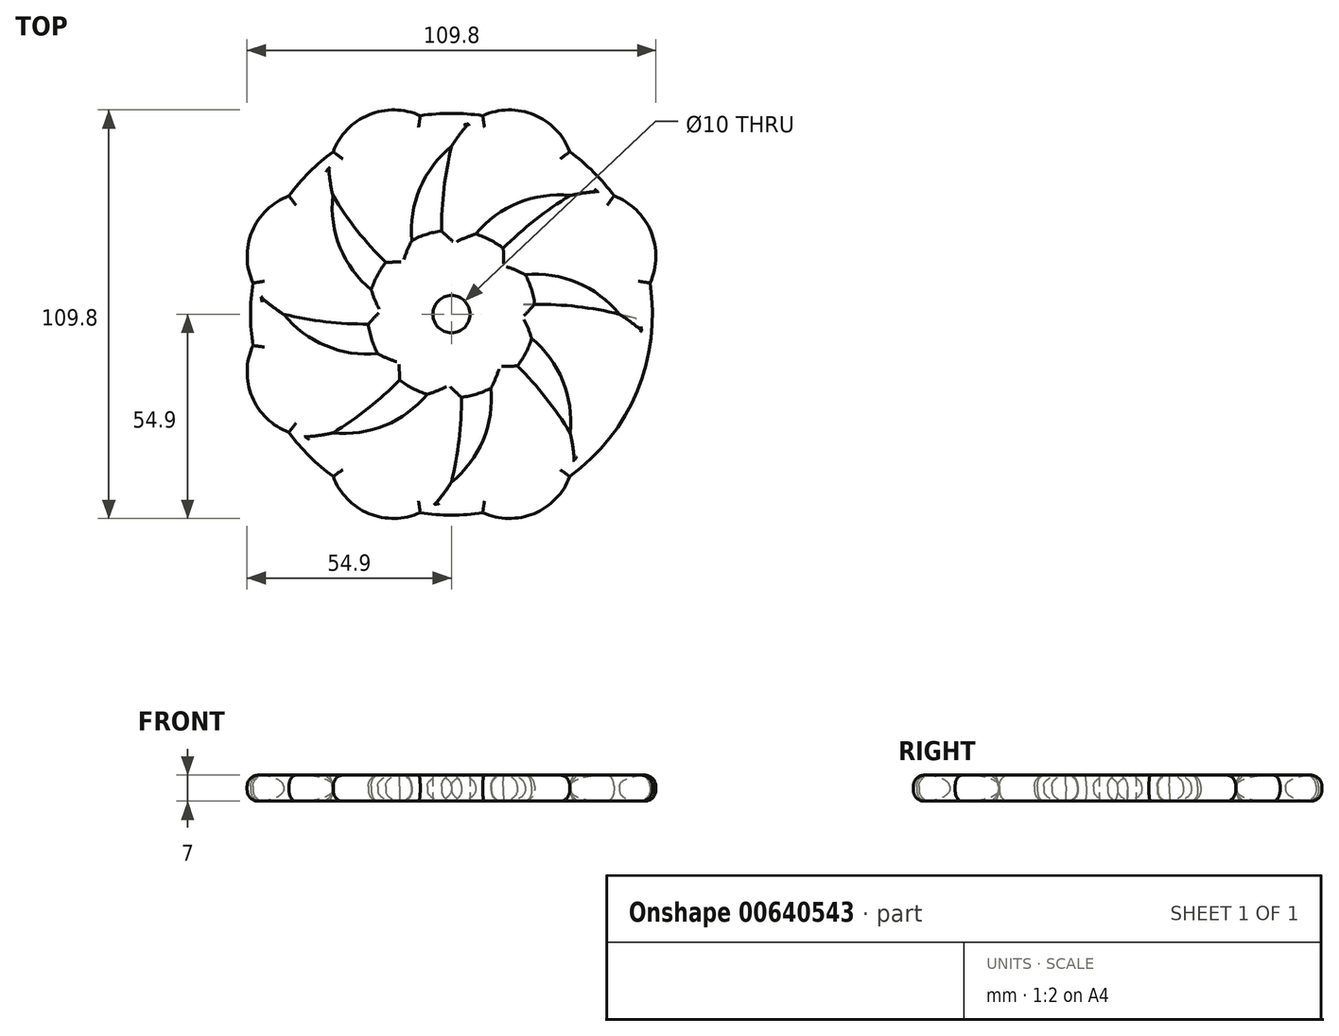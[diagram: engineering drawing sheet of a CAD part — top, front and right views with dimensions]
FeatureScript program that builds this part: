
annotation { "Feature Type Name" : "Feature", "Feature Type Description" : "" }
export const myFeature = defineFeature(function(context is Context, id is Id, definition is map)
    precondition{}
    {
        {
            var Q0;
            Q0=qCreatedBy(makeId("Top.planeOp"),FACE);
            var sketch = newSketch(context, id + "F0", { "sketchPlane" : qUnion([Q0])});
            skCircle(sketch, "E0", {"center": v(0, 0) * mm, "radius": 22.5 * mm});
            skPoint(sketch, "E1.center", {"position": v(-3, 0) * mm});
            skCircle(sketch, "E2", {"center": v(0, 0) * mm, "radius": 54 * mm});
            skCircle(sketch, "E3", {"center": v(0, 0) * mm, "radius": 5 * mm});
            skArc(sketch, "E4", {"start": v(0, 45.12) * mm, "mid": v(-10.75, 22.56) * mm, "end": v(0, 0) * mm});
            skArc(sketch, "E5", {"start": v(0, 45.12) * mm, "mid": v(-2.68, 22.56) * mm, "end": v(0, 0) * mm});
            skArc(sketch, "E6.1.0", {"start": v(-31.9, 31.9) * mm, "mid": v(-23.55, 8.35) * mm, "end": v(0, 0) * mm});
            skArc(sketch, "E6.1.1", {"start": v(-31.9, 31.9) * mm, "mid": v(-17.85, 14.06) * mm, "end": v(0, 0) * mm});
            skArc(sketch, "E6.2.0", {"start": v(-45.12, 0) * mm, "mid": v(-22.56, -10.75) * mm, "end": v(0, 0) * mm});
            skArc(sketch, "E6.2.1", {"start": v(-45.12, 0) * mm, "mid": v(-22.56, -2.68) * mm, "end": v(0, 0) * mm});
            skArc(sketch, "E6.3.0", {"start": v(-31.9, -31.9) * mm, "mid": v(-8.35, -23.55) * mm, "end": v(0, 0) * mm});
            skArc(sketch, "E6.3.1", {"start": v(-31.9, -31.9) * mm, "mid": v(-14.06, -17.85) * mm, "end": v(0, 0) * mm});
            skArc(sketch, "E6.4.0", {"start": v(0, -45.12) * mm, "mid": v(10.75, -22.56) * mm, "end": v(0, 0) * mm});
            skArc(sketch, "E6.4.1", {"start": v(0, -45.12) * mm, "mid": v(2.68, -22.56) * mm, "end": v(0, 0) * mm});
            skArc(sketch, "E6.5.0", {"start": v(31.9, -31.9) * mm, "mid": v(23.55, -8.35) * mm, "end": v(0, 0) * mm});
            skArc(sketch, "E6.5.1", {"start": v(31.9, -31.9) * mm, "mid": v(17.85, -14.06) * mm, "end": v(0, 0) * mm});
            skArc(sketch, "E6.6.0", {"start": v(45.12, 0) * mm, "mid": v(22.56, 10.75) * mm, "end": v(0, 0) * mm});
            skArc(sketch, "E6.6.1", {"start": v(45.12, 0) * mm, "mid": v(22.56, 2.68) * mm, "end": v(0, 0) * mm});
            skArc(sketch, "E6.7.0", {"start": v(31.9, 31.9) * mm, "mid": v(8.35, 23.55) * mm, "end": v(0, 0) * mm});
            skArc(sketch, "E6.7.1", {"start": v(31.9, 31.9) * mm, "mid": v(14.06, 17.85) * mm, "end": v(0, 0) * mm});
            skArc(sketch, "E7", {"start": v(-31.9, 31.9) * mm, "mid": v(-53.59, 22.2) * mm, "end": v(-45.12, 0) * mm});
            skArc(sketch, "E8.1.0", {"start": v(-45.12, 0) * mm, "mid": v(-53.59, -22.2) * mm, "end": v(-31.9, -31.9) * mm});
            skArc(sketch, "E8.2.0", {"start": v(-31.9, -31.9) * mm, "mid": v(-22.2, -53.59) * mm, "end": v(0, -45.12) * mm});
            skArc(sketch, "E8.3.0", {"start": v(0, -45.12) * mm, "mid": v(22.2, -53.59) * mm, "end": v(31.9, -31.9) * mm});
            skArc(sketch, "E8.4.0", {"start": v(31.9, -31.9) * mm, "mid": v(53.59, -22.2) * mm, "end": v(45.12, 0) * mm});
            skArc(sketch, "E8.5.0", {"start": v(45.12, 0) * mm, "mid": v(53.59, 22.2) * mm, "end": v(31.9, 31.9) * mm});
            skArc(sketch, "E8.6.0", {"start": v(31.9, 31.9) * mm, "mid": v(22.2, 53.59) * mm, "end": v(0, 45.12) * mm});
            skArc(sketch, "E8.7.0", {"start": v(0, 45.12) * mm, "mid": v(-22.2, 53.59) * mm, "end": v(-31.9, 31.9) * mm});
            skSolve(sketch);
        }
        {
            var Q0;
            {var subQ0=sQuery(id+"F0.wireOp",EDGE,"E7");var subQ1=sQuery(id+"F0.wireOp",EDGE,"E2");var subQ2=makeQuery(id+"F0.imprint","INTERSECT",VERTEX,{"disambiguationData":[OD(0.0)],"derivedFrom":[subQ1,subQ0]});Q0=makeQuery(id+"F0.imprint","IMPRINT",FACE,{"disambiguationData":[TD([[makeQuery(id+"F0.imprint","IMPRINT",EDGE,{"disambiguationData":[TD([[subQ2,-1.0]])],"derivedFrom":subQ1}),-1.0]])]});}
            var Q1;
            {var subQ3=sQuery(id+"F0.wireOp",EDGE,"E0");var subQ5=sQuery(id+"F0.wireOp",EDGE,"E6.1.0");var subQ9=makeQuery(id+"F0.imprint","INTERSECT",VERTEX,{"derivedFrom":[subQ3,subQ5]});Q1=makeQuery(id+"F0.imprint","IMPRINT",FACE,{"disambiguationData":[TD([[makeQuery(id+"F0.imprint","IMPRINT",EDGE,{"disambiguationData":[TD([[subQ9,-1.0]])],"derivedFrom":subQ3}),-1.0]])]});}
            var Q2;
            {var subQ0=sQuery(id+"F0.wireOp",EDGE,"E7");var subQ1=sQuery(id+"F0.wireOp",EDGE,"E2");var subQ2=makeQuery(id+"F0.imprint","INTERSECT",VERTEX,{"disambiguationData":[OD(1.0)],"derivedFrom":[subQ1,subQ0]});Q2=makeQuery(id+"F0.imprint","IMPRINT",FACE,{"disambiguationData":[TD([[makeQuery(id+"F0.imprint","IMPRINT",EDGE,{"disambiguationData":[TD([[subQ2,-1.0]])],"derivedFrom":subQ1}),1.0]])]});}
            var Q3;
            {var subQ1=sQuery(id+"F0.wireOp",EDGE,"E6.2.0");var subQ3=sQuery(id+"F0.wireOp",EDGE,"E0");var subQ4=makeQuery(id+"F0.imprint","INTERSECT",VERTEX,{"derivedFrom":[subQ3,subQ1]});Q3=makeQuery(id+"F0.imprint","IMPRINT",FACE,{"disambiguationData":[TD([[makeQuery(id+"F0.imprint","IMPRINT",EDGE,{"disambiguationData":[TD([[subQ4,-1.0]])],"derivedFrom":subQ3}),-1.0]])]});}
            var Q4;
            {var subQ0=sQuery(id+"F0.wireOp",EDGE,"E8.1.0");var subQ1=sQuery(id+"F0.wireOp",EDGE,"E2");var subQ2=makeQuery(id+"F0.imprint","INTERSECT",VERTEX,{"disambiguationData":[OD(0.0)],"derivedFrom":[subQ1,subQ0]});Q4=makeQuery(id+"F0.imprint","IMPRINT",FACE,{"disambiguationData":[TD([[makeQuery(id+"F0.imprint","IMPRINT",EDGE,{"disambiguationData":[TD([[subQ2,-1.0]])],"derivedFrom":subQ1}),-1.0]])]});}
            var Q5;
            {var subQ0=sQuery(id+"F0.wireOp",EDGE,"E6.2.0");var subQ1=sQuery(id+"F0.wireOp",EDGE,"E0");var subQ2=makeQuery(id+"F0.imprint","INTERSECT",VERTEX,{"derivedFrom":[subQ1,subQ0]});Q5=makeQuery(id+"F0.imprint","IMPRINT",FACE,{"disambiguationData":[TD([[makeQuery(id+"F0.imprint","IMPRINT",EDGE,{"disambiguationData":[TD([[subQ2,-1.0]])],"derivedFrom":subQ1}),1.0]])]});}
            var Q6;
            {var subQ0=sQuery(id+"F0.wireOp",EDGE,"E6.1.0");var subQ1=sQuery(id+"F0.wireOp",EDGE,"E0");var subQ2=makeQuery(id+"F0.imprint","INTERSECT",VERTEX,{"derivedFrom":[subQ1,subQ0]});Q6=makeQuery(id+"F0.imprint","IMPRINT",FACE,{"disambiguationData":[TD([[makeQuery(id+"F0.imprint","IMPRINT",EDGE,{"disambiguationData":[TD([[subQ2,-1.0]])],"derivedFrom":subQ1}),1.0]])]});}
            var Q7;
            {var subQ0=sQuery(id+"F0.wireOp",EDGE,"E4");var subQ1=sQuery(id+"F0.wireOp",EDGE,"E0");var subQ2=makeQuery(id+"F0.imprint","INTERSECT",VERTEX,{"derivedFrom":[subQ1,subQ0]});Q7=makeQuery(id+"F0.imprint","IMPRINT",FACE,{"disambiguationData":[TD([[makeQuery(id+"F0.imprint","IMPRINT",EDGE,{"disambiguationData":[TD([[subQ2,-1.0]])],"derivedFrom":subQ1}),1.0]])]});}
            var Q8;
            {var subQ3=sQuery(id+"F0.wireOp",EDGE,"E0");var subQ5=sQuery(id+"F0.wireOp",EDGE,"E4");var subQ7=makeQuery(id+"F0.imprint","INTERSECT",VERTEX,{"derivedFrom":[subQ3,subQ5]});Q8=makeQuery(id+"F0.imprint","IMPRINT",FACE,{"disambiguationData":[TD([[makeQuery(id+"F0.imprint","IMPRINT",EDGE,{"disambiguationData":[TD([[subQ7,-1.0]])],"derivedFrom":subQ3}),-1.0]])]});}
            var Q9;
            {var subQ0=sQuery(id+"F0.wireOp",EDGE,"E8.7.0");var subQ1=sQuery(id+"F0.wireOp",EDGE,"E2");var subQ2=makeQuery(id+"F0.imprint","INTERSECT",VERTEX,{"disambiguationData":[OD(0.0)],"derivedFrom":[subQ1,subQ0]});Q9=makeQuery(id+"F0.imprint","IMPRINT",FACE,{"disambiguationData":[TD([[makeQuery(id+"F0.imprint","IMPRINT",EDGE,{"disambiguationData":[TD([[subQ2,-1.0]])],"derivedFrom":subQ1}),-1.0]])]});}
            var Q10;
            {var subQ0=sQuery(id+"F0.wireOp",EDGE,"E8.6.0");var subQ1=sQuery(id+"F0.wireOp",EDGE,"E2");var subQ2=makeQuery(id+"F0.imprint","INTERSECT",VERTEX,{"disambiguationData":[OD(1.0)],"derivedFrom":[subQ1,subQ0]});Q10=makeQuery(id+"F0.imprint","IMPRINT",FACE,{"disambiguationData":[TD([[makeQuery(id+"F0.imprint","IMPRINT",EDGE,{"disambiguationData":[TD([[subQ2,-1.0]])],"derivedFrom":subQ1}),1.0]])]});}
            var Q11;
            {var subQ1=sQuery(id+"F0.wireOp",EDGE,"E6.7.0");var subQ3=sQuery(id+"F0.wireOp",EDGE,"E0");var subQ4=makeQuery(id+"F0.imprint","INTERSECT",VERTEX,{"derivedFrom":[subQ3,subQ1]});Q11=makeQuery(id+"F0.imprint","IMPRINT",FACE,{"disambiguationData":[TD([[makeQuery(id+"F0.imprint","IMPRINT",EDGE,{"disambiguationData":[TD([[subQ4,-1.0]])],"derivedFrom":subQ3}),-1.0]])]});}
            var Q12;
            {var subQ0=sQuery(id+"F0.wireOp",EDGE,"E8.6.0");var subQ1=sQuery(id+"F0.wireOp",EDGE,"E2");var subQ2=makeQuery(id+"F0.imprint","INTERSECT",VERTEX,{"disambiguationData":[OD(0.0)],"derivedFrom":[subQ1,subQ0]});Q12=makeQuery(id+"F0.imprint","IMPRINT",FACE,{"disambiguationData":[TD([[makeQuery(id+"F0.imprint","IMPRINT",EDGE,{"disambiguationData":[TD([[subQ2,-1.0]])],"derivedFrom":subQ1}),-1.0]])]});}
            var Q13;
            {var subQ0=sQuery(id+"F0.wireOp",EDGE,"E8.5.0");var subQ1=sQuery(id+"F0.wireOp",EDGE,"E2");var subQ2=makeQuery(id+"F0.imprint","INTERSECT",VERTEX,{"disambiguationData":[OD(0.0)],"derivedFrom":[subQ1,subQ0]});Q13=makeQuery(id+"F0.imprint","IMPRINT",FACE,{"disambiguationData":[TD([[makeQuery(id+"F0.imprint","IMPRINT",EDGE,{"disambiguationData":[TD([[subQ2,-1.0]])],"derivedFrom":subQ1}),1.0]])]});}
            var Q14;
            {var subQ0=sQuery(id+"F0.wireOp",EDGE,"E8.5.0");var subQ1=sQuery(id+"F0.wireOp",EDGE,"E2");var subQ2=makeQuery(id+"F0.imprint","INTERSECT",VERTEX,{"disambiguationData":[OD(0.0)],"derivedFrom":[subQ1,subQ0]});Q14=makeQuery(id+"F0.imprint","IMPRINT",FACE,{"disambiguationData":[TD([[makeQuery(id+"F0.imprint","IMPRINT",EDGE,{"disambiguationData":[TD([[subQ2,1.0]])],"derivedFrom":subQ1}),-1.0]])]});}
            var Q15;
            {var subQ0=sQuery(id+"F0.wireOp",EDGE,"E8.5.0");var subQ1=sQuery(id+"F0.wireOp",EDGE,"E2");var subQ2=makeQuery(id+"F0.imprint","INTERSECT",VERTEX,{"disambiguationData":[OD(1.0)],"derivedFrom":[subQ1,subQ0]});Q15=makeQuery(id+"F0.imprint","IMPRINT",FACE,{"disambiguationData":[TD([[makeQuery(id+"F0.imprint","IMPRINT",EDGE,{"disambiguationData":[TD([[subQ2,1.0]])],"derivedFrom":subQ1}),1.0]])]});}
            var Q16;
            {var subQ0=sQuery(id+"F0.wireOp",EDGE,"E8.4.0");var subQ1=sQuery(id+"F0.wireOp",EDGE,"E2");var subQ2=makeQuery(id+"F0.imprint","INTERSECT",VERTEX,{"disambiguationData":[OD(0.0)],"derivedFrom":[subQ1,subQ0]});Q16=makeQuery(id+"F0.imprint","IMPRINT",FACE,{"disambiguationData":[TD([[makeQuery(id+"F0.imprint","IMPRINT",EDGE,{"disambiguationData":[TD([[subQ2,-1.0]])],"derivedFrom":subQ1}),-1.0]])]});}
            var Q17;
            {var subQ0=sQuery(id+"F0.wireOp",EDGE,"E8.3.0");var subQ1=sQuery(id+"F0.wireOp",EDGE,"E2");var subQ2=makeQuery(id+"F0.imprint","INTERSECT",VERTEX,{"disambiguationData":[OD(1.0)],"derivedFrom":[subQ1,subQ0]});Q17=makeQuery(id+"F0.imprint","IMPRINT",FACE,{"disambiguationData":[TD([[makeQuery(id+"F0.imprint","IMPRINT",EDGE,{"disambiguationData":[TD([[subQ2,-1.0]])],"derivedFrom":subQ1}),1.0]])]});}
            var Q18;
            {var subQ0=sQuery(id+"F0.wireOp",EDGE,"E8.3.0");var subQ1=sQuery(id+"F0.wireOp",EDGE,"E2");var subQ2=makeQuery(id+"F0.imprint","INTERSECT",VERTEX,{"disambiguationData":[OD(0.0)],"derivedFrom":[subQ1,subQ0]});Q18=makeQuery(id+"F0.imprint","IMPRINT",FACE,{"disambiguationData":[TD([[makeQuery(id+"F0.imprint","IMPRINT",EDGE,{"disambiguationData":[TD([[subQ2,-1.0]])],"derivedFrom":subQ1}),-1.0]])]});}
            var Q19;
            {var subQ0=sQuery(id+"F0.wireOp",EDGE,"E8.2.0");var subQ1=sQuery(id+"F0.wireOp",EDGE,"E2");var subQ2=makeQuery(id+"F0.imprint","INTERSECT",VERTEX,{"disambiguationData":[OD(1.0)],"derivedFrom":[subQ1,subQ0]});Q19=makeQuery(id+"F0.imprint","IMPRINT",FACE,{"disambiguationData":[TD([[makeQuery(id+"F0.imprint","IMPRINT",EDGE,{"disambiguationData":[TD([[subQ2,-1.0]])],"derivedFrom":subQ1}),1.0]])]});}
            var Q20;
            {var subQ0=sQuery(id+"F0.wireOp",EDGE,"E8.2.0");var subQ1=sQuery(id+"F0.wireOp",EDGE,"E2");var subQ2=makeQuery(id+"F0.imprint","INTERSECT",VERTEX,{"disambiguationData":[OD(0.0)],"derivedFrom":[subQ1,subQ0]});Q20=makeQuery(id+"F0.imprint","IMPRINT",FACE,{"disambiguationData":[TD([[makeQuery(id+"F0.imprint","IMPRINT",EDGE,{"disambiguationData":[TD([[subQ2,-1.0]])],"derivedFrom":subQ1}),-1.0]])]});}
            var Q21;
            {var subQ3=sQuery(id+"F0.wireOp",EDGE,"E0");var subQ5=sQuery(id+"F0.wireOp",EDGE,"E6.3.0");var subQ7=makeQuery(id+"F0.imprint","INTERSECT",VERTEX,{"derivedFrom":[subQ3,subQ5]});Q21=makeQuery(id+"F0.imprint","IMPRINT",FACE,{"disambiguationData":[TD([[makeQuery(id+"F0.imprint","IMPRINT",EDGE,{"disambiguationData":[TD([[subQ7,-1.0]])],"derivedFrom":subQ3}),-1.0]])]});}
            var Q22;
            {var subQ0=sQuery(id+"F0.wireOp",EDGE,"E8.1.0");var subQ1=sQuery(id+"F0.wireOp",EDGE,"E2");var subQ2=makeQuery(id+"F0.imprint","INTERSECT",VERTEX,{"disambiguationData":[OD(1.0)],"derivedFrom":[subQ1,subQ0]});Q22=makeQuery(id+"F0.imprint","IMPRINT",FACE,{"disambiguationData":[TD([[makeQuery(id+"F0.imprint","IMPRINT",EDGE,{"disambiguationData":[TD([[subQ2,-1.0]])],"derivedFrom":subQ1}),1.0]])]});}
            var Q23;
            {var subQ3=sQuery(id+"F0.wireOp",EDGE,"E0");var subQ5=sQuery(id+"F0.wireOp",EDGE,"E6.4.0");var subQ7=makeQuery(id+"F0.imprint","INTERSECT",VERTEX,{"derivedFrom":[subQ3,subQ5]});Q23=makeQuery(id+"F0.imprint","IMPRINT",FACE,{"disambiguationData":[TD([[makeQuery(id+"F0.imprint","IMPRINT",EDGE,{"disambiguationData":[TD([[subQ7,-1.0]])],"derivedFrom":subQ3}),-1.0]])]});}
            var Q24;
            {var subQ1=sQuery(id+"F0.wireOp",EDGE,"E6.6.1");var subQ3=sQuery(id+"F0.wireOp",EDGE,"E0");var subQ4=makeQuery(id+"F0.imprint","INTERSECT",VERTEX,{"derivedFrom":[subQ3,subQ1]});Q24=makeQuery(id+"F0.imprint","IMPRINT",FACE,{"disambiguationData":[TD([[makeQuery(id+"F0.imprint","IMPRINT",EDGE,{"disambiguationData":[TD([[subQ4,1.0]])],"derivedFrom":subQ3}),-1.0]])]});}
            var Q25;
            {var subQ3=sQuery(id+"F0.wireOp",EDGE,"E0");var subQ8=sQuery(id+"F0.wireOp",EDGE,"E6.6.0");var subQ10=makeQuery(id+"F0.imprint","INTERSECT",VERTEX,{"derivedFrom":[subQ3,subQ8]});Q25=makeQuery(id+"F0.imprint","IMPRINT",FACE,{"disambiguationData":[TD([[makeQuery(id+"F0.imprint","IMPRINT",EDGE,{"disambiguationData":[TD([[subQ10,-1.0]])],"derivedFrom":subQ3}),-1.0]])]});}
            var Q26;
            {var subQ0=sQuery(id+"F0.wireOp",EDGE,"E6.3.0");var subQ1=sQuery(id+"F0.wireOp",EDGE,"E0");var subQ2=makeQuery(id+"F0.imprint","INTERSECT",VERTEX,{"derivedFrom":[subQ1,subQ0]});Q26=makeQuery(id+"F0.imprint","IMPRINT",FACE,{"disambiguationData":[TD([[makeQuery(id+"F0.imprint","IMPRINT",EDGE,{"disambiguationData":[TD([[subQ2,-1.0]])],"derivedFrom":subQ1}),1.0]])]});}
            var Q27;
            {var subQ0=sQuery(id+"F0.wireOp",EDGE,"E6.4.0");var subQ1=sQuery(id+"F0.wireOp",EDGE,"E0");var subQ2=makeQuery(id+"F0.imprint","INTERSECT",VERTEX,{"derivedFrom":[subQ1,subQ0]});Q27=makeQuery(id+"F0.imprint","IMPRINT",FACE,{"disambiguationData":[TD([[makeQuery(id+"F0.imprint","IMPRINT",EDGE,{"disambiguationData":[TD([[subQ2,-1.0]])],"derivedFrom":subQ1}),1.0]])]});}
            var Q28;
            {var subQ0=sQuery(id+"F0.wireOp",EDGE,"E6.6.1");var subQ1=sQuery(id+"F0.wireOp",EDGE,"E0");var subQ2=makeQuery(id+"F0.imprint","INTERSECT",VERTEX,{"derivedFrom":[subQ1,subQ0]});Q28=makeQuery(id+"F0.imprint","IMPRINT",FACE,{"disambiguationData":[TD([[makeQuery(id+"F0.imprint","IMPRINT",EDGE,{"disambiguationData":[TD([[subQ2,1.0]])],"derivedFrom":subQ1}),1.0]])]});}
            var Q29;
            {var subQ0=sQuery(id+"F0.wireOp",EDGE,"E6.6.0");var subQ1=sQuery(id+"F0.wireOp",EDGE,"E0");var subQ2=makeQuery(id+"F0.imprint","INTERSECT",VERTEX,{"derivedFrom":[subQ1,subQ0]});Q29=makeQuery(id+"F0.imprint","IMPRINT",FACE,{"disambiguationData":[TD([[makeQuery(id+"F0.imprint","IMPRINT",EDGE,{"disambiguationData":[TD([[subQ2,-1.0]])],"derivedFrom":subQ1}),1.0]])]});}
            var Q30;
            {var subQ0=sQuery(id+"F0.wireOp",EDGE,"E6.7.0");var subQ1=sQuery(id+"F0.wireOp",EDGE,"E0");var subQ2=makeQuery(id+"F0.imprint","INTERSECT",VERTEX,{"derivedFrom":[subQ1,subQ0]});Q30=makeQuery(id+"F0.imprint","IMPRINT",FACE,{"disambiguationData":[TD([[makeQuery(id+"F0.imprint","IMPRINT",EDGE,{"disambiguationData":[TD([[subQ2,-1.0]])],"derivedFrom":subQ1}),1.0]])]});}
            var Q31;
            {var subQ0=sQuery(id+"F0.wireOp",EDGE,"E6.1.1");var subQ1=sQuery(id+"F0.wireOp",EDGE,"E0");var subQ2=makeQuery(id+"F0.imprint","INTERSECT",VERTEX,{"derivedFrom":[subQ1,subQ0]});Q31=makeQuery(id+"F0.imprint","IMPRINT",FACE,{"disambiguationData":[TD([[makeQuery(id+"F0.imprint","IMPRINT",EDGE,{"disambiguationData":[TD([[subQ2,-1.0]])],"derivedFrom":subQ1}),1.0]])]});}
            var Q32;
            {var subQ0=sQuery(id+"F0.wireOp",EDGE,"E6.4.1");var subQ1=sQuery(id+"F0.wireOp",EDGE,"E0");var subQ2=makeQuery(id+"F0.imprint","INTERSECT",VERTEX,{"derivedFrom":[subQ1,subQ0]});Q32=makeQuery(id+"F0.imprint","IMPRINT",FACE,{"disambiguationData":[TD([[makeQuery(id+"F0.imprint","IMPRINT",EDGE,{"disambiguationData":[TD([[subQ2,-1.0]])],"derivedFrom":subQ1}),1.0]])]});}
            var Q33;
            {var subQ0=sQuery(id+"F0.wireOp",EDGE,"E5");var subQ1=sQuery(id+"F0.wireOp",EDGE,"E0");var subQ2=makeQuery(id+"F0.imprint","INTERSECT",VERTEX,{"derivedFrom":[subQ1,subQ0]});Q33=makeQuery(id+"F0.imprint","IMPRINT",FACE,{"disambiguationData":[TD([[makeQuery(id+"F0.imprint","IMPRINT",EDGE,{"disambiguationData":[TD([[subQ2,-1.0]])],"derivedFrom":subQ1}),1.0]])]});}
            var Q34;
            {var subQ0=sQuery(id+"F0.wireOp",EDGE,"E6.7.1");var subQ1=sQuery(id+"F0.wireOp",EDGE,"E0");var subQ2=makeQuery(id+"F0.imprint","INTERSECT",VERTEX,{"derivedFrom":[subQ1,subQ0]});Q34=makeQuery(id+"F0.imprint","IMPRINT",FACE,{"disambiguationData":[TD([[makeQuery(id+"F0.imprint","IMPRINT",EDGE,{"disambiguationData":[TD([[subQ2,-1.0]])],"derivedFrom":subQ1}),1.0]])]});}
            var Q35;
            {var subQ0=sQuery(id+"F0.wireOp",EDGE,"E6.5.1");var subQ1=sQuery(id+"F0.wireOp",EDGE,"E0");var subQ2=makeQuery(id+"F0.imprint","INTERSECT",VERTEX,{"derivedFrom":[subQ1,subQ0]});Q35=makeQuery(id+"F0.imprint","IMPRINT",FACE,{"disambiguationData":[TD([[makeQuery(id+"F0.imprint","IMPRINT",EDGE,{"disambiguationData":[TD([[subQ2,-1.0]])],"derivedFrom":subQ1}),1.0]])]});}
            var Q36;
            {var subQ0=sQuery(id+"F0.wireOp",EDGE,"E6.3.1");var subQ1=sQuery(id+"F0.wireOp",EDGE,"E0");var subQ2=makeQuery(id+"F0.imprint","INTERSECT",VERTEX,{"derivedFrom":[subQ1,subQ0]});Q36=makeQuery(id+"F0.imprint","IMPRINT",FACE,{"disambiguationData":[TD([[makeQuery(id+"F0.imprint","IMPRINT",EDGE,{"disambiguationData":[TD([[subQ2,-1.0]])],"derivedFrom":subQ1}),1.0]])]});}
            var Q37;
            {var subQ0=sQuery(id+"F0.wireOp",EDGE,"E6.2.1");var subQ1=sQuery(id+"F0.wireOp",EDGE,"E0");var subQ2=makeQuery(id+"F0.imprint","INTERSECT",VERTEX,{"derivedFrom":[subQ1,subQ0]});Q37=makeQuery(id+"F0.imprint","IMPRINT",FACE,{"disambiguationData":[TD([[makeQuery(id+"F0.imprint","IMPRINT",EDGE,{"disambiguationData":[TD([[subQ2,-1.0]])],"derivedFrom":subQ1}),1.0]])]});}
            var Q38;
            {var subQ0=sQuery(id+"F0.wireOp",EDGE,"E6.6.0");var subQ1=sQuery(id+"F0.wireOp",EDGE,"E0");var subQ2=makeQuery(id+"F0.imprint","INTERSECT",VERTEX,{"derivedFrom":[subQ1,subQ0]});Q38=makeQuery(id+"F0.imprint","IMPRINT",FACE,{"disambiguationData":[TD([[makeQuery(id+"F0.imprint","IMPRINT",EDGE,{"disambiguationData":[TD([[subQ2,1.0]])],"derivedFrom":subQ1}),1.0]])]});}
            var Q39;
            {var subQ0=sQuery(id+"F0.wireOp",EDGE,"E8.7.0");var subQ1=sQuery(id+"F0.wireOp",EDGE,"E2");var subQ2=makeQuery(id+"F0.imprint","INTERSECT",VERTEX,{"disambiguationData":[OD(1.0)],"derivedFrom":[subQ1,subQ0]});Q39=makeQuery(id+"F0.imprint","IMPRINT",FACE,{"disambiguationData":[TD([[makeQuery(id+"F0.imprint","IMPRINT",EDGE,{"disambiguationData":[TD([[subQ2,-1.0]])],"derivedFrom":subQ1}),1.0]])]});}
            extrude(context, id + "F1", {"entities" : qUnion([Q0, Q1, Q2, Q3, Q4, Q5, Q6, Q7, Q8, Q9, Q10, Q11, Q12, Q13, Q14, Q15, Q16, Q17, Q18, Q19, Q20, Q21, Q22, Q23, Q24, Q25, Q26, Q27, Q28, Q29, Q30, Q31, Q32, Q33, Q34, Q35, Q36, Q37, Q38, Q39]), "depth" : 7 * mm, "offsetDistance" : 25 * mm});
        }
        {
            var Q0;
            {var subQ0=sQuery(id+"F0.wireOp",EDGE,"E2");Q0=makeQuery(id+"F1.opExtrude","CAP_EDGE",EDGE,{"disambiguationData":[OSD([subQ0]),TDD([makeQuery(id+"F0.imprint","IMPRINT",EDGE,{"disambiguationData":[TD([[makeQuery(id+"F0.imprint","INTERSECT",VERTEX,{"disambiguationData":[OD(1.0)],"derivedFrom":[subQ0,sQuery(id+"F0.wireOp",EDGE,"E8.7.0")]}),-1.0]])],"derivedFrom":subQ0})])],"isStart":false});}
            var Q1;
            Q1=makeQuery(id+"F1.opExtrude","CAP_EDGE",EDGE,{"disambiguationData":[OSD([sQuery(id+"F0.wireOp",EDGE,"E8.7.0")])],"isStart":false});
            var Q2;
            {var subQ0=sQuery(id+"F0.wireOp",EDGE,"E2");Q2=makeQuery(id+"F1.opExtrude","CAP_EDGE",EDGE,{"disambiguationData":[OSD([subQ0]),TDD([makeQuery(id+"F0.imprint","IMPRINT",EDGE,{"disambiguationData":[TD([[makeQuery(id+"F0.imprint","INTERSECT",VERTEX,{"disambiguationData":[OD(1.0)],"derivedFrom":[subQ0,sQuery(id+"F0.wireOp",EDGE,"E8.6.0")]}),-1.0]])],"derivedFrom":subQ0})])],"isStart":false});}
            var Q3;
            Q3=makeQuery(id+"F1.opExtrude","CAP_EDGE",EDGE,{"disambiguationData":[OSD([sQuery(id+"F0.wireOp",EDGE,"E8.6.0")])],"isStart":false});
            var Q4;
            {var subQ0=sQuery(id+"F0.wireOp",EDGE,"E2");Q4=makeQuery(id+"F1.opExtrude","CAP_EDGE",EDGE,{"disambiguationData":[OSD([subQ0]),TDD([makeQuery(id+"F0.imprint","IMPRINT",EDGE,{"disambiguationData":[TD([[makeQuery(id+"F0.imprint","INTERSECT",VERTEX,{"disambiguationData":[OD(0.0)],"derivedFrom":[subQ0,sQuery(id+"F0.wireOp",EDGE,"E8.5.0")]}),-1.0]])],"derivedFrom":subQ0})])],"isStart":false});}
            var Q5;
            Q5=makeQuery(id+"F1.opExtrude","CAP_EDGE",EDGE,{"disambiguationData":[OSD([sQuery(id+"F0.wireOp",EDGE,"E8.5.0")])],"isStart":false});
            var Q6;
            {var subQ0=sQuery(id+"F0.wireOp",EDGE,"E2");Q6=makeQuery(id+"F1.opExtrude","CAP_EDGE",EDGE,{"disambiguationData":[OSD([subQ0]),TDD([makeQuery(id+"F0.imprint","IMPRINT",EDGE,{"disambiguationData":[TD([[makeQuery(id+"F0.imprint","INTERSECT",VERTEX,{"disambiguationData":[OD(1.0)],"derivedFrom":[subQ0,sQuery(id+"F0.wireOp",EDGE,"E8.5.0")]}),1.0]])],"derivedFrom":subQ0})])],"isStart":false});}
            var Q7;
            Q7=makeQuery(id+"F1.opExtrude","CAP_EDGE",EDGE,{"disambiguationData":[OSD([sQuery(id+"F0.wireOp",EDGE,"E8.4.0")])],"isStart":false});
            var Q8;
            {var subQ0=sQuery(id+"F0.wireOp",EDGE,"E2");Q8=makeQuery(id+"F1.opExtrude","CAP_EDGE",EDGE,{"disambiguationData":[OSD([subQ0]),TDD([makeQuery(id+"F0.imprint","IMPRINT",EDGE,{"disambiguationData":[TD([[makeQuery(id+"F0.imprint","INTERSECT",VERTEX,{"disambiguationData":[OD(1.0)],"derivedFrom":[subQ0,sQuery(id+"F0.wireOp",EDGE,"E8.3.0")]}),-1.0]])],"derivedFrom":subQ0})])],"isStart":false});}
            var Q9;
            Q9=makeQuery(id+"F1.opExtrude","CAP_EDGE",EDGE,{"disambiguationData":[OSD([sQuery(id+"F0.wireOp",EDGE,"E8.3.0")])],"isStart":false});
            var Q10;
            {var subQ0=sQuery(id+"F0.wireOp",EDGE,"E2");Q10=makeQuery(id+"F1.opExtrude","CAP_EDGE",EDGE,{"disambiguationData":[OSD([subQ0]),TDD([makeQuery(id+"F0.imprint","IMPRINT",EDGE,{"disambiguationData":[TD([[makeQuery(id+"F0.imprint","INTERSECT",VERTEX,{"disambiguationData":[OD(1.0)],"derivedFrom":[subQ0,sQuery(id+"F0.wireOp",EDGE,"E8.2.0")]}),-1.0]])],"derivedFrom":subQ0})])],"isStart":false});}
            var Q11;
            Q11=makeQuery(id+"F1.opExtrude","CAP_EDGE",EDGE,{"disambiguationData":[OSD([sQuery(id+"F0.wireOp",EDGE,"E8.2.0")])],"isStart":false});
            var Q12;
            {var subQ0=sQuery(id+"F0.wireOp",EDGE,"E2");Q12=makeQuery(id+"F1.opExtrude","CAP_EDGE",EDGE,{"disambiguationData":[OSD([subQ0]),TDD([makeQuery(id+"F0.imprint","IMPRINT",EDGE,{"disambiguationData":[TD([[makeQuery(id+"F0.imprint","INTERSECT",VERTEX,{"disambiguationData":[OD(1.0)],"derivedFrom":[subQ0,sQuery(id+"F0.wireOp",EDGE,"E8.1.0")]}),-1.0]])],"derivedFrom":subQ0})])],"isStart":false});}
            var Q13;
            Q13=makeQuery(id+"F1.opExtrude","CAP_EDGE",EDGE,{"disambiguationData":[OSD([sQuery(id+"F0.wireOp",EDGE,"E8.1.0")])],"isStart":false});
            var Q14;
            {var subQ0=sQuery(id+"F0.wireOp",EDGE,"E2");Q14=makeQuery(id+"F1.opExtrude","CAP_EDGE",EDGE,{"disambiguationData":[OSD([subQ0]),TDD([makeQuery(id+"F0.imprint","IMPRINT",EDGE,{"disambiguationData":[TD([[makeQuery(id+"F0.imprint","INTERSECT",VERTEX,{"disambiguationData":[OD(1.0)],"derivedFrom":[subQ0,sQuery(id+"F0.wireOp",EDGE,"E7")]}),-1.0]])],"derivedFrom":subQ0})])],"isStart":false});}
            var Q15;
            Q15=makeQuery(id+"F1.opExtrude","CAP_EDGE",EDGE,{"disambiguationData":[OSD([sQuery(id+"F0.wireOp",EDGE,"E7")])],"isStart":false});
            var Q16;
            Q16=makeQuery(id+"F1.opExtrude","CAP_EDGE",EDGE,{"disambiguationData":[OSD([sQuery(id+"F0.wireOp",EDGE,"E6.2.0")])],"isStart":false});
            var Q17;
            {var subQ0=sQuery(id+"F0.wireOp",EDGE,"E0");Q17=makeQuery(id+"F1.opExtrude","CAP_EDGE",EDGE,{"disambiguationData":[OSD([subQ0]),TDD([makeQuery(id+"F0.imprint","IMPRINT",EDGE,{"disambiguationData":[TD([[makeQuery(id+"F0.imprint","INTERSECT",VERTEX,{"derivedFrom":[subQ0,sQuery(id+"F0.wireOp",EDGE,"E6.2.1")]}),-1.0]])],"derivedFrom":subQ0})])],"isStart":false});}
            var Q18;
            Q18=makeQuery(id+"F1.opExtrude","CAP_EDGE",EDGE,{"disambiguationData":[OSD([sQuery(id+"F0.wireOp",EDGE,"E6.1.1")])],"isStart":false});
            var Q19;
            {var subQ0=sQuery(id+"F0.wireOp",EDGE,"E0");Q19=makeQuery(id+"F1.opExtrude","CAP_EDGE",EDGE,{"disambiguationData":[OSD([subQ0]),TDD([makeQuery(id+"F0.imprint","IMPRINT",EDGE,{"disambiguationData":[TD([[makeQuery(id+"F0.imprint","INTERSECT",VERTEX,{"derivedFrom":[subQ0,sQuery(id+"F0.wireOp",EDGE,"E6.1.1")]}),-1.0]])],"derivedFrom":subQ0})])],"isStart":false});}
            var Q20;
            {var subQ0=sQuery(id+"F0.wireOp",EDGE,"E0");Q20=makeQuery(id+"F1.opExtrude","CAP_EDGE",EDGE,{"disambiguationData":[OSD([subQ0]),TDD([makeQuery(id+"F0.imprint","IMPRINT",EDGE,{"disambiguationData":[TD([[makeQuery(id+"F0.imprint","INTERSECT",VERTEX,{"derivedFrom":[subQ0,sQuery(id+"F0.wireOp",EDGE,"E5")]}),-1.0]])],"derivedFrom":subQ0})])],"isStart":false});}
            var Q21;
            Q21=makeQuery(id+"F1.opExtrude","CAP_EDGE",EDGE,{"disambiguationData":[OSD([sQuery(id+"F0.wireOp",EDGE,"E4")])],"isStart":false});
            var Q22;
            Q22=makeQuery(id+"F1.opExtrude","CAP_EDGE",EDGE,{"disambiguationData":[OSD([sQuery(id+"F0.wireOp",EDGE,"E5")])],"isStart":false});
            var Q23;
            Q23=makeQuery(id+"F1.opExtrude","CAP_EDGE",EDGE,{"disambiguationData":[OSD([sQuery(id+"F0.wireOp",EDGE,"E6.7.0")])],"isStart":false});
            var Q24;
            Q24=makeQuery(id+"F1.opExtrude","CAP_EDGE",EDGE,{"disambiguationData":[OSD([sQuery(id+"F0.wireOp",EDGE,"E6.7.1")])],"isStart":false});
            var Q25;
            {var subQ0=sQuery(id+"F0.wireOp",EDGE,"E0");Q25=makeQuery(id+"F1.opExtrude","CAP_EDGE",EDGE,{"disambiguationData":[OSD([subQ0]),TDD([makeQuery(id+"F0.imprint","IMPRINT",EDGE,{"disambiguationData":[TD([[makeQuery(id+"F0.imprint","INTERSECT",VERTEX,{"derivedFrom":[subQ0,sQuery(id+"F0.wireOp",EDGE,"E6.7.1")]}),-1.0]])],"derivedFrom":subQ0})])],"isStart":false});}
            var Q26;
            Q26=makeQuery(id+"F1.opExtrude","CAP_EDGE",EDGE,{"disambiguationData":[OSD([sQuery(id+"F0.wireOp",EDGE,"E6.6.0")])],"isStart":false});
            var Q27;
            Q27=makeQuery(id+"F1.opExtrude","CAP_EDGE",EDGE,{"disambiguationData":[OSD([sQuery(id+"F0.wireOp",EDGE,"E6.6.1")])],"isStart":false});
            var Q28;
            {var subQ0=sQuery(id+"F0.wireOp",EDGE,"E0");Q28=makeQuery(id+"F1.opExtrude","CAP_EDGE",EDGE,{"disambiguationData":[OSD([subQ0]),TDD([makeQuery(id+"F0.imprint","IMPRINT",EDGE,{"disambiguationData":[TD([[makeQuery(id+"F0.imprint","INTERSECT",VERTEX,{"derivedFrom":[subQ0,sQuery(id+"F0.wireOp",EDGE,"E6.6.0")]}),1.0]])],"derivedFrom":subQ0})])],"isStart":false});}
            var Q29;
            Q29=makeQuery(id+"F1.opExtrude","CAP_EDGE",EDGE,{"disambiguationData":[OSD([sQuery(id+"F0.wireOp",EDGE,"E6.5.1")])],"isStart":false});
            var Q30;
            Q30=makeQuery(id+"F1.opExtrude","CAP_EDGE",EDGE,{"disambiguationData":[OSD([sQuery(id+"F0.wireOp",EDGE,"E6.4.0")])],"isStart":false});
            var Q31;
            {var subQ0=sQuery(id+"F0.wireOp",EDGE,"E0");Q31=makeQuery(id+"F1.opExtrude","CAP_EDGE",EDGE,{"disambiguationData":[OSD([subQ0]),TDD([makeQuery(id+"F0.imprint","IMPRINT",EDGE,{"disambiguationData":[TD([[makeQuery(id+"F0.imprint","INTERSECT",VERTEX,{"derivedFrom":[subQ0,sQuery(id+"F0.wireOp",EDGE,"E6.4.1")]}),-1.0]])],"derivedFrom":subQ0})])],"isStart":false});}
            var Q32;
            Q32=makeQuery(id+"F1.opExtrude","CAP_EDGE",EDGE,{"disambiguationData":[OSD([sQuery(id+"F0.wireOp",EDGE,"E6.4.1")])],"isStart":false});
            var Q33;
            Q33=makeQuery(id+"F1.opExtrude","CAP_EDGE",EDGE,{"disambiguationData":[OSD([sQuery(id+"F0.wireOp",EDGE,"E6.5.0")])],"isStart":false});
            var Q34;
            {var subQ0=sQuery(id+"F0.wireOp",EDGE,"E0");Q34=makeQuery(id+"F1.opExtrude","CAP_EDGE",EDGE,{"disambiguationData":[OSD([subQ0]),TDD([makeQuery(id+"F0.imprint","IMPRINT",EDGE,{"disambiguationData":[TD([[makeQuery(id+"F0.imprint","INTERSECT",VERTEX,{"derivedFrom":[subQ0,sQuery(id+"F0.wireOp",EDGE,"E6.5.1")]}),-1.0]])],"derivedFrom":subQ0})])],"isStart":false});}
            var Q35;
            {var subQ0=sQuery(id+"F0.wireOp",EDGE,"E0");Q35=makeQuery(id+"F1.opExtrude","CAP_EDGE",EDGE,{"disambiguationData":[OSD([subQ0]),TDD([makeQuery(id+"F0.imprint","IMPRINT",EDGE,{"disambiguationData":[TD([[makeQuery(id+"F0.imprint","INTERSECT",VERTEX,{"derivedFrom":[subQ0,sQuery(id+"F0.wireOp",EDGE,"E6.3.1")]}),-1.0]])],"derivedFrom":subQ0})])],"isStart":false});}
            var Q36;
            {var subQ0=sQuery(id+"F0.wireOp",EDGE,"E0");Q36=makeQuery(id+"F1.opExtrude","CAP_EDGE",EDGE,{"disambiguationData":[OSD([subQ0]),TDD([makeQuery(id+"F0.imprint","IMPRINT",EDGE,{"disambiguationData":[TD([[makeQuery(id+"F0.imprint","INTERSECT",VERTEX,{"derivedFrom":[subQ0,sQuery(id+"F0.wireOp",EDGE,"E6.3.1")]}),-1.0]])],"derivedFrom":subQ0})])],"isStart":false});}
            var Q37;
            Q37=makeQuery(id+"F1.opExtrude","CAP_EDGE",EDGE,{"disambiguationData":[OSD([sQuery(id+"F0.wireOp",EDGE,"E6.3.0")])],"isStart":false});
            var Q38;
            Q38=makeQuery(id+"F1.opExtrude","CAP_EDGE",EDGE,{"disambiguationData":[OSD([sQuery(id+"F0.wireOp",EDGE,"E6.3.1")])],"isStart":false});
            var Q39;
            Q39=makeQuery(id+"F1.opExtrude","CAP_EDGE",EDGE,{"disambiguationData":[OSD([sQuery(id+"F0.wireOp",EDGE,"E6.2.1")])],"isStart":false});
            var Q40;
            Q40=makeQuery(id+"F1.opExtrude","CAP_EDGE",EDGE,{"disambiguationData":[OSD([sQuery(id+"F0.wireOp",EDGE,"E6.1.0")])],"isStart":false});
            var Q41;
            Q41=makeQuery(id+"F1.opExtrude","CAP_EDGE",EDGE,{"disambiguationData":[OSD([sQuery(id+"F0.wireOp",EDGE,"E6.4.0")])],"isStart":true});
            var Q42;
            Q42=makeQuery(id+"F1.opExtrude","CAP_EDGE",EDGE,{"disambiguationData":[OSD([sQuery(id+"F0.wireOp",EDGE,"E6.4.1")])],"isStart":true});
            var Q43;
            {var subQ0=sQuery(id+"F0.wireOp",EDGE,"E0");Q43=makeQuery(id+"F1.opExtrude","CAP_EDGE",EDGE,{"disambiguationData":[OSD([subQ0]),TDD([makeQuery(id+"F0.imprint","IMPRINT",EDGE,{"disambiguationData":[TD([[makeQuery(id+"F0.imprint","INTERSECT",VERTEX,{"derivedFrom":[subQ0,sQuery(id+"F0.wireOp",EDGE,"E6.4.1")]}),-1.0]])],"derivedFrom":subQ0})])],"isStart":true});}
            var Q44;
            Q44=makeQuery(id+"F1.opExtrude","CAP_EDGE",EDGE,{"disambiguationData":[OSD([sQuery(id+"F0.wireOp",EDGE,"E6.3.0")])],"isStart":true});
            var Q45;
            Q45=makeQuery(id+"F1.opExtrude","CAP_EDGE",EDGE,{"disambiguationData":[OSD([sQuery(id+"F0.wireOp",EDGE,"E6.3.1")])],"isStart":true});
            var Q46;
            {var subQ0=sQuery(id+"F0.wireOp",EDGE,"E0");Q46=makeQuery(id+"F1.opExtrude","CAP_EDGE",EDGE,{"disambiguationData":[OSD([subQ0]),TDD([makeQuery(id+"F0.imprint","IMPRINT",EDGE,{"disambiguationData":[TD([[makeQuery(id+"F0.imprint","INTERSECT",VERTEX,{"derivedFrom":[subQ0,sQuery(id+"F0.wireOp",EDGE,"E6.3.1")]}),-1.0]])],"derivedFrom":subQ0})])],"isStart":true});}
            var Q47;
            Q47=makeQuery(id+"F1.opExtrude","CAP_EDGE",EDGE,{"disambiguationData":[OSD([sQuery(id+"F0.wireOp",EDGE,"E6.5.1")])],"isStart":true});
            var Q48;
            Q48=makeQuery(id+"F1.opExtrude","CAP_EDGE",EDGE,{"disambiguationData":[OSD([sQuery(id+"F0.wireOp",EDGE,"E6.5.0")])],"isStart":true});
            var Q49;
            {var subQ0=sQuery(id+"F0.wireOp",EDGE,"E0");Q49=makeQuery(id+"F1.opExtrude","CAP_EDGE",EDGE,{"disambiguationData":[OSD([subQ0]),TDD([makeQuery(id+"F0.imprint","IMPRINT",EDGE,{"disambiguationData":[TD([[makeQuery(id+"F0.imprint","INTERSECT",VERTEX,{"derivedFrom":[subQ0,sQuery(id+"F0.wireOp",EDGE,"E6.5.1")]}),-1.0]])],"derivedFrom":subQ0})])],"isStart":true});}
            var Q50;
            Q50=makeQuery(id+"F1.opExtrude","CAP_EDGE",EDGE,{"disambiguationData":[OSD([sQuery(id+"F0.wireOp",EDGE,"E8.2.0")])],"isStart":true});
            var Q51;
            {var subQ0=sQuery(id+"F0.wireOp",EDGE,"E2");Q51=makeQuery(id+"F1.opExtrude","CAP_EDGE",EDGE,{"disambiguationData":[OSD([subQ0]),TDD([makeQuery(id+"F0.imprint","IMPRINT",EDGE,{"disambiguationData":[TD([[makeQuery(id+"F0.imprint","INTERSECT",VERTEX,{"disambiguationData":[OD(1.0)],"derivedFrom":[subQ0,sQuery(id+"F0.wireOp",EDGE,"E8.2.0")]}),-1.0]])],"derivedFrom":subQ0})])],"isStart":true});}
            var Q52;
            Q52=makeQuery(id+"F1.opExtrude","CAP_EDGE",EDGE,{"disambiguationData":[OSD([sQuery(id+"F0.wireOp",EDGE,"E8.3.0")])],"isStart":true});
            var Q53;
            {var subQ0=sQuery(id+"F0.wireOp",EDGE,"E2");Q53=makeQuery(id+"F1.opExtrude","CAP_EDGE",EDGE,{"disambiguationData":[OSD([subQ0]),TDD([makeQuery(id+"F0.imprint","IMPRINT",EDGE,{"disambiguationData":[TD([[makeQuery(id+"F0.imprint","INTERSECT",VERTEX,{"disambiguationData":[OD(1.0)],"derivedFrom":[subQ0,sQuery(id+"F0.wireOp",EDGE,"E8.3.0")]}),-1.0]])],"derivedFrom":subQ0})])],"isStart":true});}
            var Q54;
            Q54=makeQuery(id+"F1.opExtrude","CAP_EDGE",EDGE,{"disambiguationData":[OSD([sQuery(id+"F0.wireOp",EDGE,"E8.4.0")])],"isStart":true});
            var Q55;
            {var subQ0=sQuery(id+"F0.wireOp",EDGE,"E2");Q55=makeQuery(id+"F1.opExtrude","CAP_EDGE",EDGE,{"disambiguationData":[OSD([subQ0]),TDD([makeQuery(id+"F0.imprint","IMPRINT",EDGE,{"disambiguationData":[TD([[makeQuery(id+"F0.imprint","INTERSECT",VERTEX,{"disambiguationData":[OD(1.0)],"derivedFrom":[subQ0,sQuery(id+"F0.wireOp",EDGE,"E8.5.0")]}),1.0]])],"derivedFrom":subQ0})])],"isStart":true});}
            var Q56;
            Q56=makeQuery(id+"F1.opExtrude","CAP_EDGE",EDGE,{"disambiguationData":[OSD([sQuery(id+"F0.wireOp",EDGE,"E8.5.0")])],"isStart":true});
            var Q57;
            {var subQ0=sQuery(id+"F0.wireOp",EDGE,"E2");Q57=makeQuery(id+"F1.opExtrude","CAP_EDGE",EDGE,{"disambiguationData":[OSD([subQ0]),TDD([makeQuery(id+"F0.imprint","IMPRINT",EDGE,{"disambiguationData":[TD([[makeQuery(id+"F0.imprint","INTERSECT",VERTEX,{"disambiguationData":[OD(0.0)],"derivedFrom":[subQ0,sQuery(id+"F0.wireOp",EDGE,"E8.5.0")]}),-1.0]])],"derivedFrom":subQ0})])],"isStart":true});}
            var Q58;
            {var subQ0=sQuery(id+"F0.wireOp",EDGE,"E2");Q58=makeQuery(id+"F1.opExtrude","CAP_EDGE",EDGE,{"disambiguationData":[OSD([subQ0]),TDD([makeQuery(id+"F0.imprint","IMPRINT",EDGE,{"disambiguationData":[TD([[makeQuery(id+"F0.imprint","INTERSECT",VERTEX,{"disambiguationData":[OD(1.0)],"derivedFrom":[subQ0,sQuery(id+"F0.wireOp",EDGE,"E8.1.0")]}),-1.0]])],"derivedFrom":subQ0})])],"isStart":true});}
            var Q59;
            Q59=makeQuery(id+"F1.opExtrude","CAP_EDGE",EDGE,{"disambiguationData":[OSD([sQuery(id+"F0.wireOp",EDGE,"E8.1.0")])],"isStart":true});
            var Q60;
            {var subQ0=sQuery(id+"F0.wireOp",EDGE,"E2");Q60=makeQuery(id+"F1.opExtrude","CAP_EDGE",EDGE,{"disambiguationData":[OSD([subQ0]),TDD([makeQuery(id+"F0.imprint","IMPRINT",EDGE,{"disambiguationData":[TD([[makeQuery(id+"F0.imprint","INTERSECT",VERTEX,{"disambiguationData":[OD(1.0)],"derivedFrom":[subQ0,sQuery(id+"F0.wireOp",EDGE,"E7")]}),-1.0]])],"derivedFrom":subQ0})])],"isStart":true});}
            var Q61;
            Q61=makeQuery(id+"F1.opExtrude","CAP_EDGE",EDGE,{"disambiguationData":[OSD([sQuery(id+"F0.wireOp",EDGE,"E7")])],"isStart":true});
            var Q62;
            {var subQ0=sQuery(id+"F0.wireOp",EDGE,"E2");Q62=makeQuery(id+"F1.opExtrude","CAP_EDGE",EDGE,{"disambiguationData":[OSD([subQ0]),TDD([makeQuery(id+"F0.imprint","IMPRINT",EDGE,{"disambiguationData":[TD([[makeQuery(id+"F0.imprint","INTERSECT",VERTEX,{"disambiguationData":[OD(1.0)],"derivedFrom":[subQ0,sQuery(id+"F0.wireOp",EDGE,"E8.7.0")]}),-1.0]])],"derivedFrom":subQ0})])],"isStart":true});}
            var Q63;
            Q63=makeQuery(id+"F1.opExtrude","CAP_EDGE",EDGE,{"disambiguationData":[OSD([sQuery(id+"F0.wireOp",EDGE,"E6.1.0")])],"isStart":true});
            var Q64;
            {var subQ0=sQuery(id+"F0.wireOp",EDGE,"E0");Q64=makeQuery(id+"F1.opExtrude","CAP_EDGE",EDGE,{"disambiguationData":[OSD([subQ0]),TDD([makeQuery(id+"F0.imprint","IMPRINT",EDGE,{"disambiguationData":[TD([[makeQuery(id+"F0.imprint","INTERSECT",VERTEX,{"derivedFrom":[subQ0,sQuery(id+"F0.wireOp",EDGE,"E6.1.1")]}),-1.0]])],"derivedFrom":subQ0})])],"isStart":true});}
            var Q65;
            Q65=makeQuery(id+"F1.opExtrude","CAP_EDGE",EDGE,{"disambiguationData":[OSD([sQuery(id+"F0.wireOp",EDGE,"E6.1.1")])],"isStart":true});
            var Q66;
            Q66=makeQuery(id+"F1.opExtrude","CAP_EDGE",EDGE,{"disambiguationData":[OSD([sQuery(id+"F0.wireOp",EDGE,"E6.2.1")])],"isStart":true});
            var Q67;
            Q67=makeQuery(id+"F1.opExtrude","CAP_EDGE",EDGE,{"disambiguationData":[OSD([sQuery(id+"F0.wireOp",EDGE,"E6.2.0")])],"isStart":true});
            var Q68;
            {var subQ0=sQuery(id+"F0.wireOp",EDGE,"E0");Q68=makeQuery(id+"F1.opExtrude","CAP_EDGE",EDGE,{"disambiguationData":[OSD([subQ0]),TDD([makeQuery(id+"F0.imprint","IMPRINT",EDGE,{"disambiguationData":[TD([[makeQuery(id+"F0.imprint","INTERSECT",VERTEX,{"derivedFrom":[subQ0,sQuery(id+"F0.wireOp",EDGE,"E6.2.1")]}),-1.0]])],"derivedFrom":subQ0})])],"isStart":true});}
            var Q69;
            Q69=makeQuery(id+"F1.opExtrude","CAP_EDGE",EDGE,{"disambiguationData":[OSD([sQuery(id+"F0.wireOp",EDGE,"E8.7.0")])],"isStart":true});
            var Q70;
            {var subQ0=sQuery(id+"F0.wireOp",EDGE,"E2");Q70=makeQuery(id+"F1.opExtrude","CAP_EDGE",EDGE,{"disambiguationData":[OSD([subQ0]),TDD([makeQuery(id+"F0.imprint","IMPRINT",EDGE,{"disambiguationData":[TD([[makeQuery(id+"F0.imprint","INTERSECT",VERTEX,{"disambiguationData":[OD(1.0)],"derivedFrom":[subQ0,sQuery(id+"F0.wireOp",EDGE,"E8.6.0")]}),-1.0]])],"derivedFrom":subQ0})])],"isStart":true});}
            var Q71;
            Q71=makeQuery(id+"F1.opExtrude","CAP_EDGE",EDGE,{"disambiguationData":[OSD([sQuery(id+"F0.wireOp",EDGE,"E8.6.0")])],"isStart":true});
            var Q72;
            Q72=makeQuery(id+"F1.opExtrude","CAP_EDGE",EDGE,{"disambiguationData":[OSD([sQuery(id+"F0.wireOp",EDGE,"E4")])],"isStart":true});
            var Q73;
            Q73=makeQuery(id+"F1.opExtrude","CAP_EDGE",EDGE,{"disambiguationData":[OSD([sQuery(id+"F0.wireOp",EDGE,"E5")])],"isStart":true});
            var Q74;
            {var subQ0=sQuery(id+"F0.wireOp",EDGE,"E0");Q74=makeQuery(id+"F1.opExtrude","CAP_EDGE",EDGE,{"disambiguationData":[OSD([subQ0]),TDD([makeQuery(id+"F0.imprint","IMPRINT",EDGE,{"disambiguationData":[TD([[makeQuery(id+"F0.imprint","INTERSECT",VERTEX,{"derivedFrom":[subQ0,sQuery(id+"F0.wireOp",EDGE,"E5")]}),-1.0]])],"derivedFrom":subQ0})])],"isStart":true});}
            var Q75;
            {var subQ0=sQuery(id+"F0.wireOp",EDGE,"E0");Q75=makeQuery(id+"F1.opExtrude","CAP_EDGE",EDGE,{"disambiguationData":[OSD([subQ0]),TDD([makeQuery(id+"F0.imprint","IMPRINT",EDGE,{"disambiguationData":[TD([[makeQuery(id+"F0.imprint","INTERSECT",VERTEX,{"derivedFrom":[subQ0,sQuery(id+"F0.wireOp",EDGE,"E6.7.1")]}),-1.0]])],"derivedFrom":subQ0})])],"isStart":true});}
            var Q76;
            Q76=makeQuery(id+"F1.opExtrude","CAP_EDGE",EDGE,{"disambiguationData":[OSD([sQuery(id+"F0.wireOp",EDGE,"E6.7.1")])],"isStart":true});
            var Q77;
            Q77=makeQuery(id+"F1.opExtrude","CAP_EDGE",EDGE,{"disambiguationData":[OSD([sQuery(id+"F0.wireOp",EDGE,"E6.7.0")])],"isStart":true});
            var Q78;
            {var subQ0=sQuery(id+"F0.wireOp",EDGE,"E0");Q78=makeQuery(id+"F1.opExtrude","CAP_EDGE",EDGE,{"disambiguationData":[OSD([subQ0]),TDD([makeQuery(id+"F0.imprint","IMPRINT",EDGE,{"disambiguationData":[TD([[makeQuery(id+"F0.imprint","INTERSECT",VERTEX,{"derivedFrom":[subQ0,sQuery(id+"F0.wireOp",EDGE,"E6.6.0")]}),1.0]])],"derivedFrom":subQ0})])],"isStart":true});}
            var Q79;
            Q79=makeQuery(id+"F1.opExtrude","CAP_EDGE",EDGE,{"disambiguationData":[OSD([sQuery(id+"F0.wireOp",EDGE,"E6.6.0")])],"isStart":true});
            fillet(context, id + "F2", {"entities" : qUnion([Q0, Q1, Q2, Q3, Q4, Q5, Q6, Q7, Q8, Q9, Q10, Q11, Q12, Q13, Q14, Q15, Q16, Q17, Q18, Q19, Q20, Q21, Q22, Q23, Q24, Q25, Q26, Q27, Q28, Q29, Q30, Q31, Q32, Q33, Q34, Q35, Q36, Q37, Q38, Q39, Q40, Q41, Q42, Q43, Q44, Q45, Q46, Q47, Q48, Q49, Q50, Q51, Q52, Q53, Q54, Q55, Q56, Q57, Q58, Q59, Q60, Q61, Q62, Q63, Q64, Q65, Q66, Q67, Q68, Q69, Q70, Q71, Q72, Q73, Q74, Q75, Q76, Q77, Q78, Q79]), "radius" : 3 * mm, "tangentPropagation" : true, "allowEdgeOverflow" : false});
        }
    });
